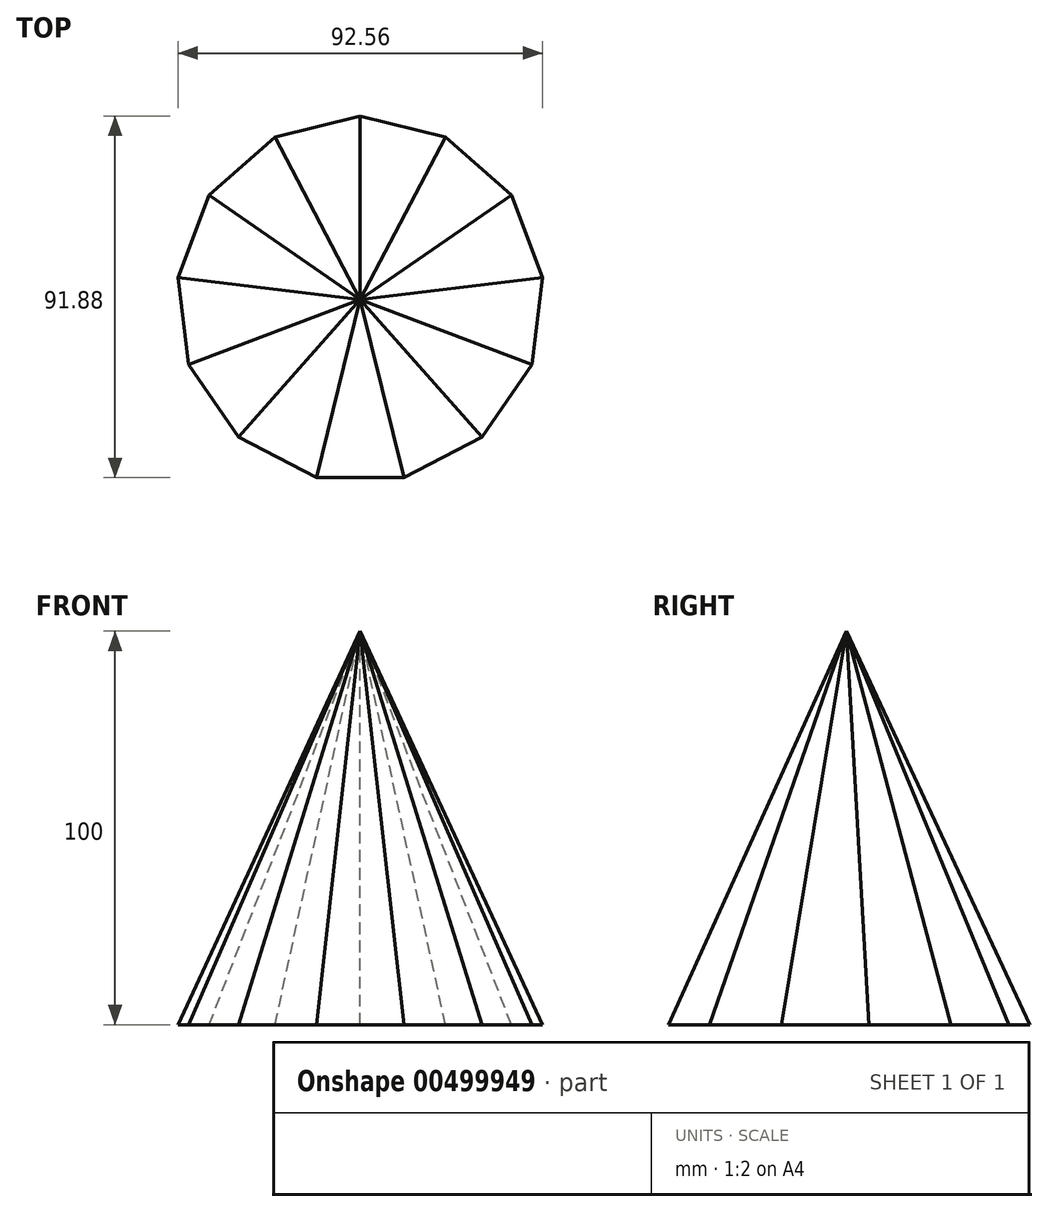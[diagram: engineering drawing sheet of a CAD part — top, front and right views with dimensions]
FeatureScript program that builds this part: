
annotation { "Feature Type Name" : "Feature", "Feature Type Description" : "" }
export const myFeature = defineFeature(function(context is Context, id is Id, definition is map)
    precondition{}
    {
        {
            var Q0;
            Q0=qCreatedBy(makeId("Top.planeOp"),FACE);
            var sketch = newSketch(context, id + "F0", { "sketchPlane" : qUnion([Q0])});
            skCircle(sketch, "E0.cCircle", {"center": v(0, 0) * mm, "radius": 46.62 * mm, "construction": true});
            skLineSegment(sketch, "E0.0", {"start": v(0, 46.62) * mm, "end": v(21.66, 41.28) * mm});
            skLineSegment(sketch, "E0.1", {"start": v(21.66, 41.28) * mm, "end": v(38.37, 26.48) * mm});
            skLineSegment(sketch, "E0.2", {"start": v(38.37, 26.48) * mm, "end": v(46.28, 5.62) * mm});
            skLineSegment(sketch, "E0.3", {"start": v(46.28, 5.62) * mm, "end": v(43.59, -16.53) * mm});
            skLineSegment(sketch, "E0.4", {"start": v(43.59, -16.53) * mm, "end": v(30.91, -34.9) * mm});
            skLineSegment(sketch, "E0.5", {"start": v(30.91, -34.9) * mm, "end": v(11.16, -45.26) * mm});
            skLineSegment(sketch, "E0.6", {"start": v(11.16, -45.26) * mm, "end": v(-11.16, -45.26) * mm});
            skLineSegment(sketch, "E0.7", {"start": v(-11.16, -45.26) * mm, "end": v(-30.91, -34.9) * mm});
            skLineSegment(sketch, "E0.8", {"start": v(-30.91, -34.9) * mm, "end": v(-43.59, -16.53) * mm});
            skLineSegment(sketch, "E0.9", {"start": v(-43.59, -16.53) * mm, "end": v(-46.28, 5.62) * mm});
            skLineSegment(sketch, "E0.10", {"start": v(-46.28, 5.62) * mm, "end": v(-38.37, 26.48) * mm});
            skLineSegment(sketch, "E0.11", {"start": v(-38.37, 26.48) * mm, "end": v(-21.66, 41.28) * mm});
            skLineSegment(sketch, "E0.12", {"start": v(-21.66, 41.28) * mm, "end": v(0, 46.62) * mm});
            skSolve(sketch);
        }
        {
            var Q0;
            Q0=qCreatedBy(makeId("Top.planeOp"),FACE);
            cPlane(context, id + "F1", {"entities" : qUnion([Q0]), "cplaneType" : CPlaneType.OFFSET, "offset" : 100 * mm, "width" : 150 * mm, "height" : 150 * mm});
        }
        {
            var Q0;
            Q0=qCreatedBy(id+"F1.planeOp",FACE);
            var sketch = newSketch(context, id + "F2", { "sketchPlane" : qUnion([Q0])});
            skPoint(sketch, "E1", {"position": v(0, 0) * mm});
            skSolve(sketch);
        }
        {
            var Q0;
            Q0=makeQuery(id+"F0.imprint","IMPRINT",FACE,{"disambiguationData":[TD([[makeQuery(id+"F0.imprint","IMPRINT",EDGE,{"derivedFrom":sQuery(id+"F0.wireOp",EDGE,"E0.0")}),-1.0]])]});
            var Q1;
            Q1=sQuery(id+"F2.wireOp",VERTEX,"E1");
            loft(context, id + "F3", {"sheetProfilesArray" : [{ "sheetProfileEntities" : qUnion([Q0]) }, { "sheetProfileEntities" : qUnion([Q1]) }]});
        }
    });
